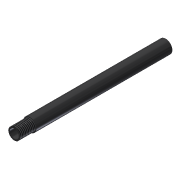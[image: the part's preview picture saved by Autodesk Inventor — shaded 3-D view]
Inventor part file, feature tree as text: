
AUTODESK INVENTOR PART (.ipt)
format: ipt  version: 2014 SP1 (Build 180222100, 222)  size: 84,480 bytes
history: native  units: in
note: dims shown in document units (in); Inventor stores cm internally (conversion verified against a paired STEP export)
features: extrude x2, sketch x2, thread x1
ambient origin geometry x8: Origin, YZ Plane, XZ Plane, XY Plane, X Axis, Y Axis, Z Axis, Center Point
bodies: Solid1 (feature_tree)
feature tree (5):
  extrude  "Extrusion1"  Depth=0.857in
  extrude  "Extrusion2"  Depth=1.0in TaperAngle=0.0deg
  thread  "Thread2"  [1 undecoded]
  sketch  "Sketch1"  dims[d0=0.584in d1=0.857in]
  sketch  "Sketch2"  dims[d2=9.75in d3=0.0in d4=1.0in d5=0.0in d11=1.0in d12=0.0in]
note: 1 required parameter value undecoded (feature->parameter linkage not recoverable at this tier; creation-order binding heuristic only, values carry confidence <= 0.55)
